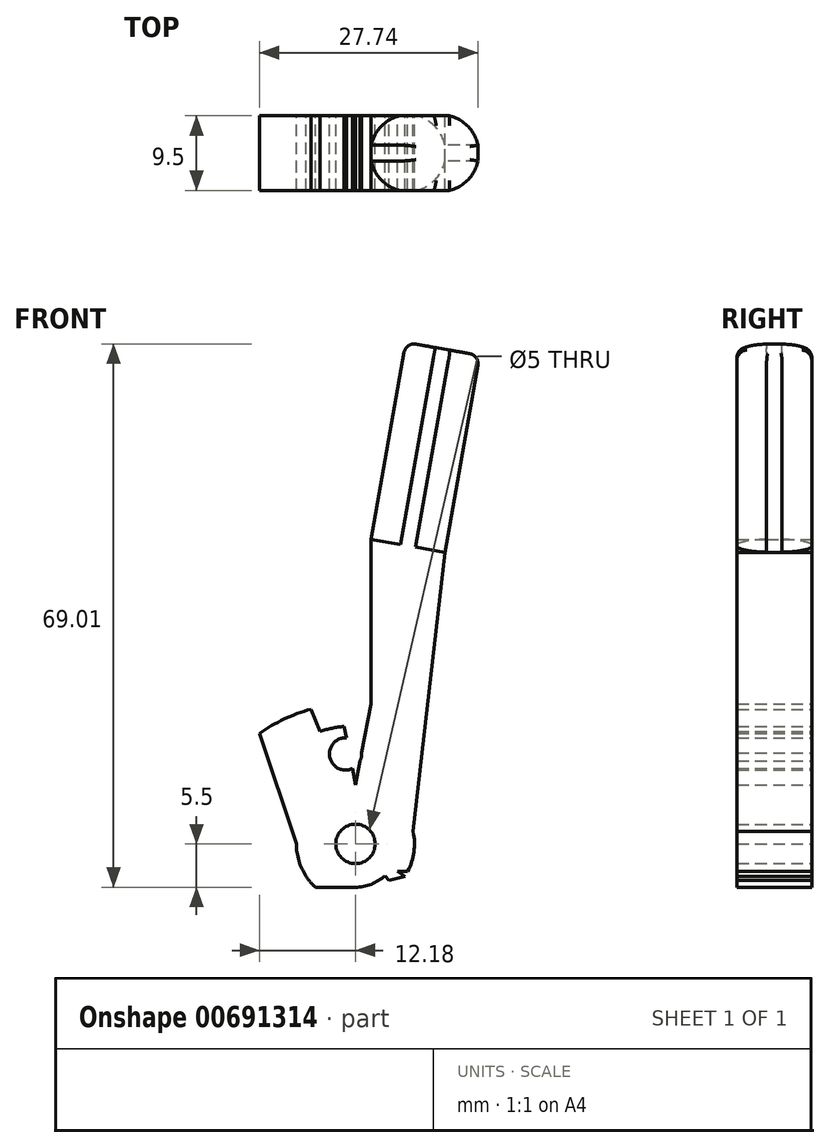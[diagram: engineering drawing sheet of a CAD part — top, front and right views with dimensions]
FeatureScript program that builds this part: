
annotation { "Feature Type Name" : "Feature", "Feature Type Description" : "" }
export const myFeature = defineFeature(function(context is Context, id is Id, definition is map)
    precondition{}
    {
        {
            var Q0;
            Q0=qCreatedBy(makeId("Front.planeOp"),FACE);
            var sketch = newSketch(context, id + "F0", { "sketchPlane" : qUnion([Q0])});
            skLineSegment(sketch, "E0.bottom", {"start": v(-21.33, 17.9) * mm, "end": v(21.47, 17.9) * mm, "construction": true});
            skLineSegment(sketch, "E0.top", {"start": v(-21.33, -7.5) * mm, "end": v(21.47, -7.5) * mm});
            skLineSegment(sketch, "E0.left", {"start": v(-21.33, 17.9) * mm, "end": v(-21.33, -7.5) * mm, "construction": true});
            skLineSegment(sketch, "E0.right", {"start": v(21.47, 17.9) * mm, "end": v(21.47, -7.5) * mm});
            skCircle(sketch, "E1", {"center": v(0, 0) * mm, "radius": 2.5 * mm});
            skCircle(sketch, "E2", {"center": v(0, 0) * mm, "radius": 7.5 * mm});
            skLineSegment(sketch, "E3", {"start": v(0, 0) * mm, "end": v(13.06, 74.1) * mm, "construction": true});
            skLineSegment(sketch, "E4", {"start": v(-2, 68.93) * mm, "end": v(-2, 31.5) * mm, "construction": true});
            skLineSegment(sketch, "E5", {"start": v(2, 68.93) * mm, "end": v(2, 31.34) * mm, "construction": true});
            skLineSegment(sketch, "E6", {"start": v(10.99, 62.3) * mm, "end": v(6.3, 63.13) * mm});
            skLineSegment(sketch, "E7.MirrorCS", {"start": v(10.99, 62.3) * mm, "end": v(15.66, 61.48) * mm});
            skLineSegment(sketch, "E8", {"start": v(6.3, 63.13) * mm, "end": v(2, 38.7) * mm});
            skLineSegment(sketch, "E9", {"start": v(2, 38.7) * mm, "end": v(11.36, 37.05) * mm});
            skPoint(sketch, "E9.endSnap0", {"position": v(6.53, 37.05) * mm});
            skLineSegment(sketch, "E10", {"start": v(11.36, 37.05) * mm, "end": v(15.66, 61.48) * mm});
            skLineSegment(sketch, "E11", {"start": v(0, 0) * mm, "end": v(50.73, 10.78) * mm, "construction": true});
            skLineSegment(sketch, "E12", {"start": v(11.36, 37.05) * mm, "end": v(7.34, 1.56) * mm});
            skLineSegment(sketch, "E13", {"start": v(2, 38.7) * mm, "end": v(2, 17.81) * mm});
            skLineSegment(sketch, "E14", {"start": v(-2, 14.87) * mm, "end": v(-2, 31.5) * mm});
            skCircle(sketch, "E15", {"center": v(0, 0) * mm, "radius": 38.75 * mm, "construction": true});
            skLineSegment(sketch, "E16", {"start": v(0, 0) * mm, "end": v(11.36, 37.05) * mm, "construction": true});
            skLineSegment(sketch, "E17", {"start": v(0, 0) * mm, "end": v(22.66, 40.8) * mm, "construction": true});
            skLineSegment(sketch, "E18", {"start": v(18.81, 33.88) * mm, "end": v(7.5, 0) * mm});
            skLineSegment(sketch, "E19", {"start": v(0, 0) * mm, "end": v(-31.78, 57.3) * mm, "construction": true});
            skArc(sketch, "E20", {"start": v(-2, 14.87) * mm, "mid": v(0, 15) * mm, "end": v(2, 14.87) * mm});
            skLineSegment(sketch, "E21", {"start": v(-49.76, -3.5) * mm, "end": v(40.68, -3.5) * mm, "construction": true});
            skLineSegment(sketch, "E22", {"start": v(-46.54, -5.5) * mm, "end": v(40.68, -5.5) * mm, "construction": true});
            skCircle(sketch, "E23", {"center": v(0, 0) * mm, "radius": 5.5 * mm, "construction": true});
            skLineSegment(sketch, "E24", {"start": v(-18.8, 33.89) * mm, "end": v(-7.5, 0) * mm});
            skLineSegment(sketch, "E25", {"start": v(-21.33, -3.5) * mm, "end": v(21.47, -3.5) * mm});
            skLineSegment(sketch, "E26", {"start": v(-21.33, 17.9) * mm, "end": v(21.47, 17.9) * mm});
            skArc(sketch, "E27", {"start": v(21.47, -3.5) * mm, "mid": v(0.07, 17.9) * mm, "end": v(-21.33, -3.5) * mm});
            skLineSegment(sketch, "E28", {"start": v(2, 17.81) * mm, "end": v(2, 14.87) * mm});
            skLineSegment(sketch, "E29", {"start": v(-5.1, -5.5) * mm, "end": v(5.1, -5.5) * mm});
            skLineSegment(sketch, "E30.MirrorCS", {"start": v(0, 0) * mm, "end": v(-50.73, 10.78) * mm, "construction": true});
            skLineSegment(sketch, "E31", {"start": v(-18.8, 33.89) * mm, "end": v(-9.98, 37.44) * mm});
            skLineSegment(sketch, "E32", {"start": v(-14.39, 35.66) * mm, "end": v(-23.71, 58.78) * mm, "construction": true});
            skLineSegment(sketch, "E33", {"start": v(-9.98, 37.44) * mm, "end": v(-19.05, 59.91) * mm, "construction": true});
            skPoint(sketch, "E33.endSnap0", {"position": v(-19.05, 47.22) * mm});
            skArc(sketch, "E34", {"start": v(2, 14.87) * mm, "mid": v(-1.28, 14.95) * mm, "end": v(-4.5, 14.31) * mm});
            skArc(sketch, "E35", {"start": v(4.24, -3.5) * mm, "mid": v(0, -5.5) * mm, "end": v(-4.24, -3.5) * mm});
            skLineSegment(sketch, "E36", {"start": v(0, 0) * mm, "end": v(5.1, -5.5) * mm});
            skLineSegment(sketch, "E37", {"start": v(0, 0) * mm, "end": v(6.28, -4.1) * mm});
            skLineSegment(sketch, "E38", {"start": v(6.28, -4.1) * mm, "end": v(1.33, -5.34) * mm});
            skLineSegment(sketch, "E39.MirrorCS", {"start": v(0, 0) * mm, "end": v(-6.28, -4.1) * mm});
            skLineSegment(sketch, "E40", {"start": v(-6.28, -4.1) * mm, "end": v(-1.33, -5.34) * mm});
            skLineSegment(sketch, "E41", {"start": v(2, 17.81) * mm, "end": v(0, 7.5) * mm});
            skLineSegment(sketch, "E42", {"start": v(0, 7.5) * mm, "end": v(-2, 17.8) * mm});
            skLineSegment(sketch, "E43", {"start": v(0, 7.5) * mm, "end": v(7.34, 1.56) * mm});
            skLineSegment(sketch, "E44", {"start": v(-9.98, 37.44) * mm, "end": v(-15.4, 62.98) * mm, "construction": true});
            skLineSegment(sketch, "E45", {"start": v(-13.22, 62.33) * mm, "end": v(-1.56, 7.34) * mm, "construction": true});
            skLineSegment(sketch, "E46", {"start": v(-9.98, 37.44) * mm, "end": v(-5.67, 17.12) * mm});
            skLineSegment(sketch, "E47", {"start": v(-5.67, 17.12) * mm, "end": v(-1.56, 7.34) * mm});
            skLineSegment(sketch, "E48", {"start": v(-12.18, 14.05) * mm, "end": v(8.88, 16) * mm, "construction": true});
            skLineSegment(sketch, "E49", {"start": v(-7.5, 0) * mm, "end": v(7.34, 1.56) * mm, "construction": true});
            skLineSegment(sketch, "E50", {"start": v(-1.65, 15.02) * mm, "end": v(-0.08, 0.78) * mm, "construction": true});
            skLineSegment(sketch, "E51", {"start": v(0, 0) * mm, "end": v(-1.25, 11.43) * mm, "construction": true});
            skCircle(sketch, "E52", {"center": v(-1.25, 11.43) * mm, "radius": 2.05 * mm});
            skLineSegment(sketch, "E53", {"start": v(-6.28, -17.07) * mm, "end": v(-6.28, -28.9) * mm, "construction": true});
            skLineSegment(sketch, "E54", {"start": v(7.5, 0) * mm, "end": v(7.5, -24.83) * mm, "construction": true});
            skSolve(sketch);
        }
        {
            var Q0;
            {var subQ3=sQuery(id+"F0.wireOp",EDGE,"E24");var subQ5=sQuery(id+"F0.wireOp",EDGE,"E2");var subQ6=makeQuery(id+"F0.imprint","INTERSECT",VERTEX,{"derivedFrom":[subQ5,subQ3]});Q0=makeQuery(id+"F0.imprint","IMPRINT",FACE,{"disambiguationData":[TD([[makeQuery(id+"F0.imprint","IMPRINT",EDGE,{"disambiguationData":[TD([[subQ6,1.0]])],"derivedFrom":subQ5}),-1.0]])]});}
            var Q1;
            {var subQ3=sQuery(id+"F0.wireOp",EDGE,"E34");var subQ5=makeQuery(id+"F0.imprint","INTERSECT",VERTEX,{"derivedFrom":[sQuery(id+"F0.wireOp",EDGE,"E14"),subQ3]});Q1=makeQuery(id+"F0.imprint","IMPRINT",FACE,{"disambiguationData":[TD([[makeQuery(id+"F0.imprint","IMPRINT",EDGE,{"disambiguationData":[TD([[subQ5,1.0]])],"derivedFrom":subQ3}),1.0]])]});}
            var Q2;
            {var subQ0=sQuery(id+"F0.wireOp",EDGE,"E41");var subQ1=sQuery(id+"F0.wireOp",EDGE,"E34");var subQ2=makeQuery(id+"F0.imprint","INTERSECT",VERTEX,{"derivedFrom":[subQ1,subQ0]});Q2=makeQuery(id+"F0.imprint","IMPRINT",FACE,{"disambiguationData":[TD([[makeQuery(id+"F0.imprint","IMPRINT",EDGE,{"disambiguationData":[TD([[subQ2,-1.0]])],"derivedFrom":subQ1}),1.0]])]});}
            var Q3;
            {var subQ0=sQuery(id+"F0.wireOp",EDGE,"E28");Q3=makeQuery(id+"F0.imprint","IMPRINT",FACE,{"disambiguationData":[TD([[makeQuery(id+"F0.imprint","IMPRINT",EDGE,{"derivedFrom":subQ0}),-1.0]])]});}
            var Q4;
            {var subQ12=sQuery(id+"F0.wireOp",EDGE,"E28");Q4=makeQuery(id+"F0.imprint","IMPRINT",FACE,{"disambiguationData":[TD([[makeQuery(id+"F0.imprint","IMPRINT",EDGE,{"derivedFrom":subQ12}),1.0]])]});}
            var Q5;
            {var subQ0=sQuery(id+"F0.wireOp",EDGE,"E9");Q5=makeQuery(id+"F0.imprint","IMPRINT",FACE,{"disambiguationData":[TD([[makeQuery(id+"F0.imprint","IMPRINT",EDGE,{"derivedFrom":subQ0}),-1.0]])]});}
            var Q6;
            {var subQ0=sQuery(id+"F0.wireOp",EDGE,"E26");var subQ1=sQuery(id+"F0.wireOp",EDGE,"E12");var subQ2=makeQuery(id+"F0.imprint","INTERSECT",VERTEX,{"derivedFrom":[subQ1,subQ0]});Q6=makeQuery(id+"F0.imprint","IMPRINT",FACE,{"disambiguationData":[TD([[makeQuery(id+"F0.imprint","IMPRINT",EDGE,{"disambiguationData":[TD([[subQ2,-1.0]])],"derivedFrom":subQ1}),-1.0]])]});}
            var Q7;
            {var subQ3=sQuery(id+"F0.wireOp",EDGE,"E43");Q7=makeQuery(id+"F0.imprint","IMPRINT",FACE,{"disambiguationData":[TD([[makeQuery(id+"F0.imprint","IMPRINT",EDGE,{"derivedFrom":subQ3}),-1.0]])]});}
            var Q8;
            {var subQ0=sQuery(id+"F0.wireOp",EDGE,"E43");Q8=makeQuery(id+"F0.imprint","IMPRINT",FACE,{"disambiguationData":[TD([[makeQuery(id+"F0.imprint","IMPRINT",EDGE,{"derivedFrom":subQ0}),1.0]])]});}
            var Q9;
            {var subQ3=sQuery(id+"F0.wireOp",EDGE,"E1");var subQ5=sQuery(id+"F0.wireOp",EDGE,"E36");var subQ9=makeQuery(id+"F0.imprint","INTERSECT",VERTEX,{"derivedFrom":[subQ3,subQ5]});Q9=makeQuery(id+"F0.imprint","IMPRINT",FACE,{"disambiguationData":[TD([[makeQuery(id+"F0.imprint","IMPRINT",EDGE,{"disambiguationData":[TD([[subQ9,-1.0]])],"derivedFrom":subQ3}),-1.0]])]});}
            var Q10;
            {var subQ0=sQuery(id+"F0.wireOp",EDGE,"E35");var subQ4=sQuery(id+"F0.wireOp",EDGE,"E25");var subQ5=makeQuery(id+"F0.imprint","INTERSECT",VERTEX,{"disambiguationData":[OD(0.0)],"derivedFrom":[subQ4,subQ0]});Q10=makeQuery(id+"F0.imprint","IMPRINT",FACE,{"disambiguationData":[TD([[makeQuery(id+"F0.imprint","IMPRINT",EDGE,{"disambiguationData":[TD([[subQ5,1.0]])],"derivedFrom":subQ4}),-1.0]])]});}
            var Q11;
            {var subQ4=sQuery(id+"F0.wireOp",EDGE,"E36");var subQ5=sQuery(id+"F0.wireOp",EDGE,"E1");var subQ6=makeQuery(id+"F0.imprint","INTERSECT",VERTEX,{"derivedFrom":[subQ5,subQ4]});Q11=makeQuery(id+"F0.imprint","IMPRINT",FACE,{"disambiguationData":[TD([[makeQuery(id+"F0.imprint","IMPRINT",EDGE,{"disambiguationData":[TD([[subQ6,1.0]])],"derivedFrom":subQ5}),-1.0]])]});}
            var Q12;
            {var subQ0=sQuery(id+"F0.wireOp",EDGE,"E35");var subQ1=sQuery(id+"F0.wireOp",EDGE,"E25");var subQ2=makeQuery(id+"F0.imprint","INTERSECT",VERTEX,{"disambiguationData":[OD(1.0)],"derivedFrom":[subQ1,subQ0]});Q12=makeQuery(id+"F0.imprint","IMPRINT",FACE,{"disambiguationData":[TD([[makeQuery(id+"F0.imprint","IMPRINT",EDGE,{"disambiguationData":[TD([[subQ2,1.0]])],"derivedFrom":subQ1}),-1.0]])]});}
            var Q13;
            {var subQ0=sQuery(id+"F0.wireOp",EDGE,"E35");var subQ1=sQuery(id+"F0.wireOp",EDGE,"E25");var subQ2=makeQuery(id+"F0.imprint","INTERSECT",VERTEX,{"disambiguationData":[OD(0.0)],"derivedFrom":[subQ1,subQ0]});Q13=makeQuery(id+"F0.imprint","IMPRINT",FACE,{"disambiguationData":[TD([[makeQuery(id+"F0.imprint","IMPRINT",EDGE,{"disambiguationData":[TD([[subQ2,-1.0]])],"derivedFrom":subQ1}),-1.0]])]});}
            var Q14;
            {var subQ0=sQuery(id+"F0.wireOp",EDGE,"E36");var subQ1=sQuery(id+"F0.wireOp",EDGE,"E25");var subQ2=makeQuery(id+"F0.imprint","INTERSECT",VERTEX,{"derivedFrom":[subQ1,subQ0]});Q14=makeQuery(id+"F0.imprint","IMPRINT",FACE,{"disambiguationData":[TD([[makeQuery(id+"F0.imprint","IMPRINT",EDGE,{"disambiguationData":[TD([[subQ2,-1.0]])],"derivedFrom":subQ1}),-1.0]])]});}
            var Q15;
            {var subQ0=sQuery(id+"F0.wireOp",EDGE,"E29");var subQ1=sQuery(id+"F0.wireOp",EDGE,"E2");var subQ2=makeQuery(id+"F0.imprint","INTERSECT",VERTEX,{"derivedFrom":[subQ1,subQ0]});Q15=makeQuery(id+"F0.imprint","IMPRINT",FACE,{"disambiguationData":[TD([[makeQuery(id+"F0.imprint","IMPRINT",EDGE,{"disambiguationData":[TD([[subQ2,1.0]])],"derivedFrom":subQ1}),1.0]])]});}
            var Q16;
            {var subQ0=sQuery(id+"F0.wireOp",EDGE,"E39.MirrorCS");var subQ1=sQuery(id+"F0.wireOp",EDGE,"E2");var subQ2=makeQuery(id+"F0.imprint","INTERSECT",VERTEX,{"derivedFrom":[subQ1,subQ0]});Q16=makeQuery(id+"F0.imprint","IMPRINT",FACE,{"disambiguationData":[TD([[makeQuery(id+"F0.imprint","IMPRINT",EDGE,{"disambiguationData":[TD([[subQ2,-1.0]])],"derivedFrom":subQ1}),1.0]])]});}
            var Q17;
            {var subQ1=sQuery(id+"F0.wireOp",EDGE,"E2");var subQ3=sQuery(id+"F0.wireOp",EDGE,"E47");var subQ4=makeQuery(id+"F0.imprint","INTERSECT",VERTEX,{"derivedFrom":[subQ1,subQ3]});Q17=makeQuery(id+"F0.imprint","IMPRINT",FACE,{"disambiguationData":[TD([[makeQuery(id+"F0.imprint","IMPRINT",EDGE,{"disambiguationData":[TD([[subQ4,1.0]])],"derivedFrom":subQ3}),1.0]])]});}
            var Q18;
            {var subQ1=sQuery(id+"F0.wireOp",EDGE,"E41");var subQ3=sQuery(id+"F0.wireOp",EDGE,"E52");var subQ4=makeQuery(id+"F0.imprint","INTERSECT",VERTEX,{"disambiguationData":[OD(1.0)],"derivedFrom":[subQ1,subQ3]});Q18=makeQuery(id+"F0.imprint","IMPRINT",FACE,{"disambiguationData":[TD([[makeQuery(id+"F0.imprint","IMPRINT",EDGE,{"disambiguationData":[TD([[subQ4,1.0]])],"derivedFrom":subQ3}),-1.0]])]});}
            var Q19;
            {var subQ0=sQuery(id+"F0.wireOp",EDGE,"E25");var subQ2=sQuery(id+"F0.wireOp",EDGE,"E1");var subQ3=makeQuery(id+"F0.imprint","INTERSECT",VERTEX,{"disambiguationData":[OD(0.0)],"derivedFrom":[subQ2,subQ0]});Q19=makeQuery(id+"F0.imprint","IMPRINT",FACE,{"disambiguationData":[TD([[makeQuery(id+"F0.imprint","IMPRINT",EDGE,{"disambiguationData":[TD([[subQ3,1.0]])],"derivedFrom":subQ2}),-1.0]])]});}
            var Q20;
            {var subQ0=sQuery(id+"F0.wireOp",EDGE,"E34");var subQ1=sQuery(id+"F0.wireOp",EDGE,"E28");var subQ2=makeQuery(id+"F0.imprint","INTERSECT",VERTEX,{"derivedFrom":[subQ1,subQ0]});Q20=makeQuery(id+"F0.imprint","IMPRINT",FACE,{"disambiguationData":[TD([[makeQuery(id+"F0.imprint","IMPRINT",EDGE,{"disambiguationData":[TD([[subQ2,1.0]])],"derivedFrom":subQ1}),1.0]])]});}
            var Q21;
            {var subQ0=sQuery(id+"F0.wireOp",EDGE,"E34");var subQ1=sQuery(id+"F0.wireOp",EDGE,"E28");var subQ2=makeQuery(id+"F0.imprint","INTERSECT",VERTEX,{"derivedFrom":[subQ1,subQ0]});Q21=makeQuery(id+"F0.imprint","IMPRINT",FACE,{"disambiguationData":[TD([[makeQuery(id+"F0.imprint","IMPRINT",EDGE,{"disambiguationData":[TD([[subQ2,1.0]])],"derivedFrom":subQ1}),-1.0]])]});}
            var Q22;
            {var subQ0=sQuery(id+"F0.wireOp",EDGE,"E35");var subQ6=sQuery(id+"F0.wireOp",EDGE,"E25");var subQ7=makeQuery(id+"F0.imprint","INTERSECT",VERTEX,{"disambiguationData":[OD(1.0)],"derivedFrom":[subQ6,subQ0]});Q22=makeQuery(id+"F0.imprint","IMPRINT",FACE,{"disambiguationData":[TD([[makeQuery(id+"F0.imprint","IMPRINT",EDGE,{"disambiguationData":[TD([[subQ7,-1.0]])],"derivedFrom":subQ6}),-1.0]])]});}
            var Q23;
            {var subQ0=sQuery(id+"F0.wireOp",EDGE,"E38");var subQ1=sQuery(id+"F0.wireOp",EDGE,"E35");var subQ2=makeQuery(id+"F0.imprint","INTERSECT",VERTEX,{"derivedFrom":[subQ1,subQ0]});Q23=makeQuery(id+"F0.imprint","IMPRINT",FACE,{"disambiguationData":[TD([[makeQuery(id+"F0.imprint","IMPRINT",EDGE,{"disambiguationData":[TD([[subQ2,1.0]])],"derivedFrom":subQ1}),1.0]])]});}
            var Q24;
            {var subQ1=sQuery(id+"F0.wireOp",EDGE,"E2");var subQ3=sQuery(id+"F0.wireOp",EDGE,"E25");var subQ4=makeQuery(id+"F0.imprint","INTERSECT",VERTEX,{"disambiguationData":[OD(1.0)],"derivedFrom":[subQ1,subQ3]});Q24=makeQuery(id+"F0.imprint","IMPRINT",FACE,{"disambiguationData":[TD([[makeQuery(id+"F0.imprint","IMPRINT",EDGE,{"disambiguationData":[TD([[subQ4,1.0]])],"derivedFrom":subQ3}),-1.0]])]});}
            var Q25;
            {var subQ0=sQuery(id+"F0.wireOp",EDGE,"E40");var subQ1=sQuery(id+"F0.wireOp",EDGE,"E2");var subQ2=makeQuery(id+"F0.imprint","INTERSECT",VERTEX,{"derivedFrom":[subQ1,subQ0]});Q25=makeQuery(id+"F0.imprint","IMPRINT",FACE,{"disambiguationData":[TD([[makeQuery(id+"F0.imprint","IMPRINT",EDGE,{"disambiguationData":[TD([[subQ2,1.0]])],"derivedFrom":subQ1}),1.0]])]});}
            extrude(context, id + "F1", {"entities" : qUnion([Q0, Q1, Q2, Q3, Q4, Q5, Q6, Q7, Q8, Q9, Q10, Q11, Q12, Q13, Q14, Q15, Q16, Q17, Q18, Q19, Q20, Q21, Q22, Q23, Q24, Q25]), "depth" : 9.5 * mm, "offsetDistance" : 25.4 * mm});
        }
        {
            var Q0;
            Q0=makeQuery(id+"F1.opExtrude","SWEPT_FACE",FACE,{"disambiguationData":[OSD([sQuery(id+"F0.wireOp",EDGE,"E9")])]});
            var sketch = newSketch(context, id + "F2", { "sketchPlane" : qUnion([Q0])});
            skCircle(sketch, "E55", {"center": v(0, -4.75) * mm, "radius": 4.85 * mm});
            skPoint(sketch, "E55.centerSnap0", {"position": v(-4.75, -4.75) * mm});
            skSolve(sketch);
        }
        {
            var Q0;
            {var subQ0=sQuery(id+"F2.wireOp",EDGE,"E55");var subQ1=sQuery(id+"F0.wireOp",EDGE,"E9");var subQ10=makeQuery(id+"F1.opExtrude","CAP_EDGE",EDGE,{"disambiguationData":[OSD([subQ1])],"isStart":true});var subQ14=makeQuery(id+"F2.imprint","INTERSECT",VERTEX,{"disambiguationData":[OD(0.0)],"derivedFrom":[subQ10,subQ0]});Q0=makeQuery(id+"F2.imprint","IMPRINT",FACE,{"disambiguationData":[TD([[makeQuery(id+"F2.imprint","IMPRINT",EDGE,{"disambiguationData":[TD([[subQ14,1.0]])],"derivedFrom":subQ10}),-1.0]])]});}
            extrude(context, id + "F3", {"entities" : qUnion([Q0]), "operationType" : NewBodyOperationType.ADD, "depth" : 25.4 * mm, "offsetDistance" : 25.4 * mm});
        }
        {
            var Q0;
            {var subQ0=sQuery(id+"F2.wireOp",EDGE,"E55");var subQ1=sQuery(id+"F0.wireOp",EDGE,"E9");Q0=makeQuery(id+"F3.opExtrude","CAP_EDGE",EDGE,{"disambiguationData":[OSD([subQ0]),TDD([makeQuery(id+"F2.imprint","IMPRINT",EDGE,{"disambiguationData":[TD([[makeQuery(id+"F2.imprint","INTERSECT",VERTEX,{"disambiguationData":[OD(1.0)],"derivedFrom":[makeQuery(id+"F1.opExtrude","CAP_EDGE",EDGE,{"disambiguationData":[OSD([subQ1])],"isStart":true}),subQ0]}),-1.0]])],"derivedFrom":subQ0})])],"isStart":false});}
            var Q1;
            {var subQ0=sQuery(id+"F2.wireOp",EDGE,"E55");var subQ1=sQuery(id+"F0.wireOp",EDGE,"E9");Q1=makeQuery(id+"F3.opExtrude","CAP_EDGE",EDGE,{"disambiguationData":[OSD([subQ0]),TDD([makeQuery(id+"F2.imprint","IMPRINT",EDGE,{"disambiguationData":[TD([[makeQuery(id+"F2.imprint","INTERSECT",VERTEX,{"disambiguationData":[OD(0.0)],"derivedFrom":[makeQuery(id+"F1.opExtrude","CAP_EDGE",EDGE,{"disambiguationData":[OSD([subQ1])],"isStart":false}),subQ0]}),1.0]])],"derivedFrom":subQ0})])],"isStart":false});}
            var Q2;
            {var subQ0=sQuery(id+"F2.wireOp",EDGE,"E55");var subQ1=sQuery(id+"F0.wireOp",EDGE,"E9");Q2=makeQuery(id+"F3.opExtrude","CAP_EDGE",EDGE,{"disambiguationData":[OSD([subQ0]),TDD([makeQuery(id+"F2.imprint","IMPRINT",EDGE,{"disambiguationData":[TD([[makeQuery(id+"F2.imprint","INTERSECT",VERTEX,{"disambiguationData":[OD(1.0)],"derivedFrom":[makeQuery(id+"F1.opExtrude","CAP_EDGE",EDGE,{"disambiguationData":[OSD([subQ1])],"isStart":false}),subQ0]}),-1.0]])],"derivedFrom":subQ0})])],"isStart":false});}
            var Q3;
            {var subQ0=sQuery(id+"F2.wireOp",EDGE,"E55");var subQ1=sQuery(id+"F0.wireOp",EDGE,"E9");Q3=makeQuery(id+"F3.opExtrude","CAP_EDGE",EDGE,{"disambiguationData":[OSD([subQ0]),TDD([makeQuery(id+"F2.imprint","IMPRINT",EDGE,{"disambiguationData":[TD([[makeQuery(id+"F2.imprint","INTERSECT",VERTEX,{"disambiguationData":[OD(0.0)],"derivedFrom":[makeQuery(id+"F1.opExtrude","CAP_EDGE",EDGE,{"disambiguationData":[OSD([subQ1])],"isStart":true}),subQ0]}),1.0]])],"derivedFrom":subQ0})])],"isStart":false});}
            var Q4;
            Q4=makeQuery(id+"F3.opExtrude","CAP_EDGE",EDGE,{"disambiguationData":[OSD([sQuery(id+"F0.wireOp",EDGE,"E8"),sQuery(id+"F0.wireOp",EDGE,"E9"),sQuery(id+"F0.wireOp",EDGE,"E13"),sQuery(id+"F0.wireOp",EDGE,"E15")])],"isStart":false});
            var Q5;
            {var subQ0=sQuery(id+"F2.wireOp",EDGE,"E55");var subQ1=sQuery(id+"F0.wireOp",EDGE,"E9");var subQ2=makeQuery(id+"F1.opExtrude","CAP_EDGE",EDGE,{"disambiguationData":[OSD([subQ1])],"isStart":false});Q5=makeQuery(id+"F3.opExtrude","CAP_EDGE",EDGE,{"disambiguationData":[OSD([subQ1]),TDD([makeQuery(id+"F2.imprint","IMPRINT",EDGE,{"disambiguationData":[TD([[makeQuery(id+"F2.imprint","INTERSECT",VERTEX,{"disambiguationData":[OD(0.0)],"derivedFrom":[subQ2,subQ0]}),-1.0]])],"derivedFrom":subQ2})])],"isStart":false});}
            var Q6;
            Q6=makeQuery(id+"F3.opExtrude","CAP_EDGE",EDGE,{"disambiguationData":[OSD([sQuery(id+"F0.wireOp",EDGE,"E9"),sQuery(id+"F0.wireOp",EDGE,"E10"),sQuery(id+"F0.wireOp",EDGE,"E12"),sQuery(id+"F0.wireOp",EDGE,"E15")])],"isStart":false});
            var Q7;
            {var subQ0=sQuery(id+"F2.wireOp",EDGE,"E55");var subQ1=sQuery(id+"F0.wireOp",EDGE,"E9");var subQ2=makeQuery(id+"F1.opExtrude","CAP_EDGE",EDGE,{"disambiguationData":[OSD([subQ1])],"isStart":true});Q7=makeQuery(id+"F3.opExtrude","CAP_EDGE",EDGE,{"disambiguationData":[OSD([subQ1]),TDD([makeQuery(id+"F2.imprint","IMPRINT",EDGE,{"disambiguationData":[TD([[makeQuery(id+"F2.imprint","INTERSECT",VERTEX,{"disambiguationData":[OD(0.0)],"derivedFrom":[subQ2,subQ0]}),1.0]])],"derivedFrom":subQ2})])],"isStart":false});}
            fillet(context, id + "F4", {"entities" : qUnion([Q0, Q1, Q2, Q3, Q4, Q5, Q6, Q7]), "radius" : 1.27 * mm, "tangentPropagation" : true, "allowEdgeOverflow" : false});
        }
    });
